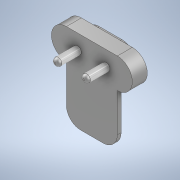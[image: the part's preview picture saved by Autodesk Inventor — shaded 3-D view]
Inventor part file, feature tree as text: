
AUTODESK INVENTOR PART (.ipt)
format: ipt  version: 2022 (Build 260153000, 153)  size: 194,560 bytes
history: native  units: in
note: dims shown in document units (in); Inventor stores cm internally (conversion verified against a paired STEP export)
features: extrude x6, sketch x6, fillet x1
ambient origin geometry x8: Origin, YZ Plane, XZ Plane, XY Plane, X Axis, Y Axis, Z Axis, Center Point
bodies: Body1 (feature_tree)
feature tree (13):
  extrude  "Extrusion2"  Depth=0.5906in
  extrude  "Extrusion3"  Depth=1.283in
  sketch  "Sketch4"  dims[d10=0.3937in d11=0.0in d12=0.0in]
  extrude  "Extrusion7"  TaperAngle=0.0deg  [1 undecoded]
  extrude  "Extrusion6"  Depth=0.315in
  extrude  "Extrusion8"  Depth=2.1091in
  extrude  "Extrusion9"  Depth=0.0984in
  fillet  "Fillet1"  Radius=0.3937in
  sketch  "Sketch2"  dims[d5=0.374in d6=0.5906in]
  sketch  "Sketch3"  dims[d7=0.4921in d8=0.0in d9=1.283in]
  sketch  "Sketch8"  dims[d13=0.5906in d14=0.315in]
  sketch  "Sketch10"  dims[d21=1.0in d22=0.0in d23=2.1091in]
  sketch  "Sketch11"  dims[d25=0.0591in d26=0.0984in d27=0.3937in d28=0.0in d29=0.752in d30=0.1984in d31=0.0in d32=0.0in d33=0.3937in d34=0.0in d35=0.5906in d36=0.0in d37=0.0787in d40=0.0in d38=0.0in d39=0.0in]
note: 1 required parameter value undecoded (feature->parameter linkage not recoverable at this tier; creation-order binding heuristic only, values carry confidence <= 0.55)
